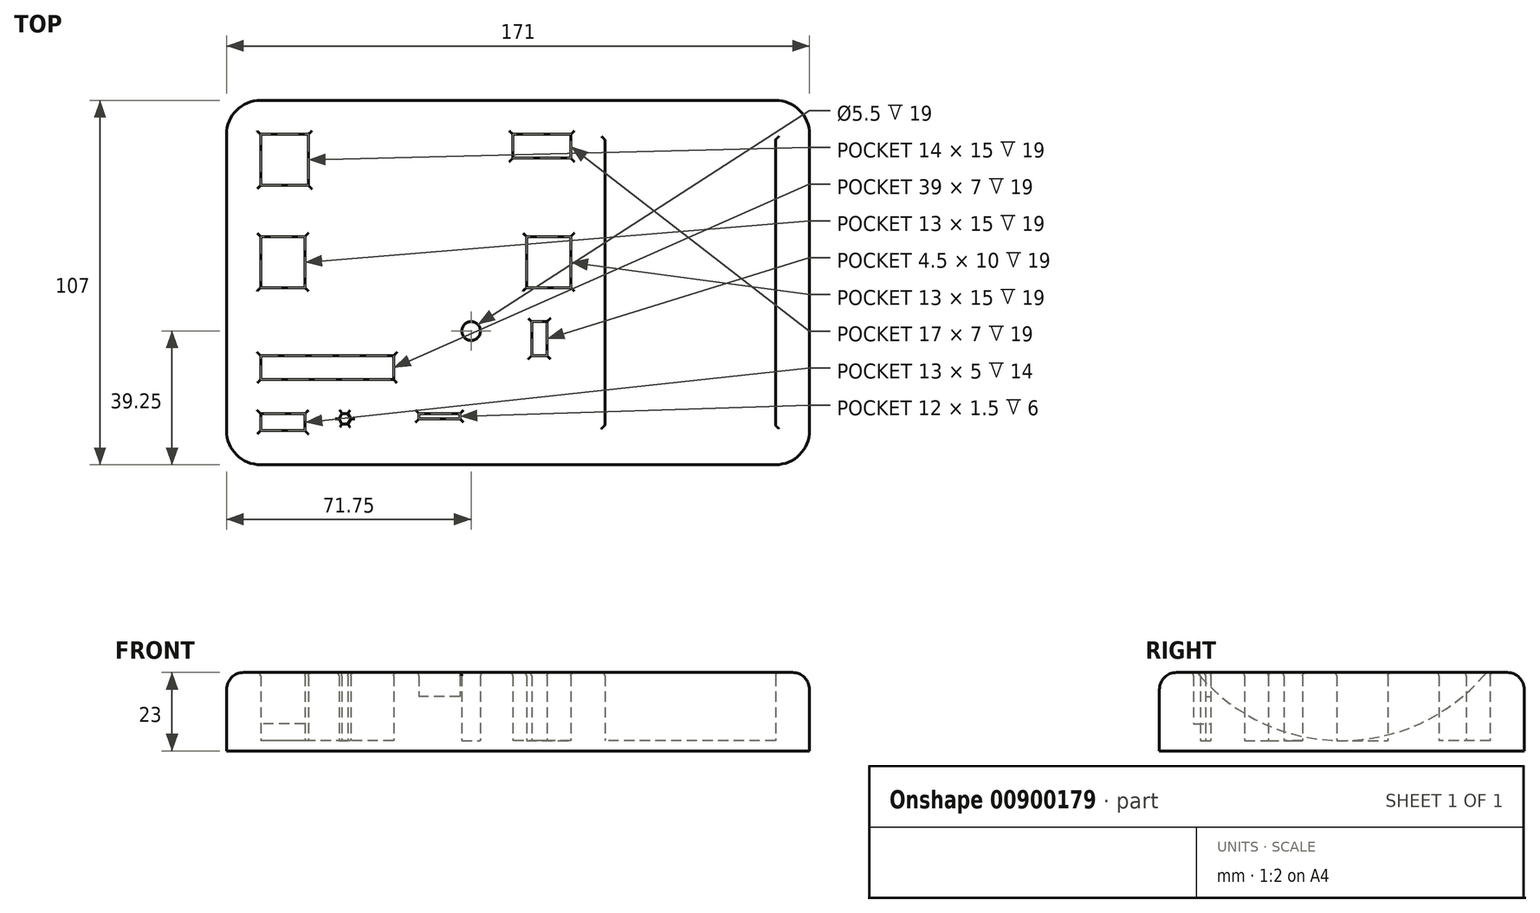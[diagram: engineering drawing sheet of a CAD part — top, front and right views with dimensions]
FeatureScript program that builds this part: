
annotation { "Feature Type Name" : "Feature", "Feature Type Description" : "" }
export const myFeature = defineFeature(function(context is Context, id is Id, definition is map)
    precondition{}
    {
        {
            var Q0;
            Q0=qCreatedBy(makeId("Top.planeOp"),FACE);
            var sketch = newSketch(context, id + "F0", { "sketchPlane" : qUnion([Q0])});
            skLineSegment(sketch, "E0.bottom", {"start": v(0, 0) * mm, "end": v(111, 0) * mm});
            skLineSegment(sketch, "E0.top", {"start": v(0, 107) * mm, "end": v(111, 107) * mm});
            skLineSegment(sketch, "E0.left", {"start": v(0, 0) * mm, "end": v(0, 107) * mm});
            skLineSegment(sketch, "E0.right", {"start": v(111, 0) * mm, "end": v(111, 107) * mm});
            skLineSegment(sketch, "E1.bottom", {"start": v(10, 82) * mm, "end": v(24, 82) * mm});
            skLineSegment(sketch, "E1.top", {"start": v(10, 97) * mm, "end": v(24, 97) * mm});
            skLineSegment(sketch, "E1.left", {"start": v(10, 82) * mm, "end": v(10, 97) * mm});
            skLineSegment(sketch, "E1.right", {"start": v(24, 82) * mm, "end": v(24, 97) * mm});
            skLineSegment(sketch, "E2.bottom", {"start": v(84, 90) * mm, "end": v(101, 90) * mm});
            skLineSegment(sketch, "E2.top", {"start": v(84, 97) * mm, "end": v(101, 97) * mm});
            skLineSegment(sketch, "E2.left", {"start": v(84, 90) * mm, "end": v(84, 97) * mm});
            skLineSegment(sketch, "E2.right", {"start": v(101, 90) * mm, "end": v(101, 97) * mm});
            skLineSegment(sketch, "E3.bottom", {"start": v(10, 32) * mm, "end": v(49, 32) * mm});
            skLineSegment(sketch, "E3.top", {"start": v(10, 25) * mm, "end": v(49, 25) * mm});
            skLineSegment(sketch, "E3.left", {"start": v(10, 32) * mm, "end": v(10, 25) * mm});
            skLineSegment(sketch, "E3.right", {"start": v(49, 32) * mm, "end": v(49, 25) * mm});
            skLineSegment(sketch, "E4.bottom", {"start": v(10, 67) * mm, "end": v(23, 67) * mm});
            skLineSegment(sketch, "E4.top", {"start": v(10, 52) * mm, "end": v(23, 52) * mm});
            skLineSegment(sketch, "E4.left", {"start": v(10, 67) * mm, "end": v(10, 52) * mm});
            skLineSegment(sketch, "E4.right", {"start": v(23, 67) * mm, "end": v(23, 52) * mm});
            skLineSegment(sketch, "E5.bottom", {"start": v(101, 67) * mm, "end": v(88, 67) * mm});
            skLineSegment(sketch, "E5.top", {"start": v(101, 52) * mm, "end": v(88, 52) * mm});
            skLineSegment(sketch, "E5.left", {"start": v(101, 67) * mm, "end": v(101, 52) * mm});
            skLineSegment(sketch, "E5.right", {"start": v(88, 67) * mm, "end": v(88, 52) * mm});
            skCircle(sketch, "E6", {"center": v(71.75, 39.25) * mm, "radius": 2.75 * mm});
            skLineSegment(sketch, "E7.bottom", {"start": v(89.5, 42) * mm, "end": v(94, 42) * mm});
            skLineSegment(sketch, "E7.top", {"start": v(89.5, 32) * mm, "end": v(94, 32) * mm});
            skLineSegment(sketch, "E7.left", {"start": v(89.5, 42) * mm, "end": v(89.5, 32) * mm});
            skLineSegment(sketch, "E7.right", {"start": v(94, 42) * mm, "end": v(94, 32) * mm});
            skLineSegment(sketch, "E8.bottom", {"start": v(10, 15) * mm, "end": v(23, 15) * mm});
            skLineSegment(sketch, "E8.top", {"start": v(10, 10) * mm, "end": v(23, 10) * mm});
            skLineSegment(sketch, "E8.left", {"start": v(10, 15) * mm, "end": v(10, 10) * mm});
            skLineSegment(sketch, "E8.right", {"start": v(23, 15) * mm, "end": v(23, 10) * mm});
            skCircle(sketch, "E9.cCircle", {"center": v(34.73, 13.5) * mm, "radius": 1.5 * mm, "construction": true});
            skLineSegment(sketch, "E9.0", {"start": v(36.46, 13.5) * mm, "end": v(35.6, 12) * mm});
            skLineSegment(sketch, "E9.1", {"start": v(35.6, 12) * mm, "end": v(33.87, 12) * mm});
            skLineSegment(sketch, "E9.2", {"start": v(33.87, 12) * mm, "end": v(33, 13.5) * mm});
            skLineSegment(sketch, "E9.3", {"start": v(33, 13.5) * mm, "end": v(33.87, 15) * mm});
            skLineSegment(sketch, "E9.4", {"start": v(33.87, 15) * mm, "end": v(35.6, 15) * mm});
            skLineSegment(sketch, "E9.5", {"start": v(35.6, 15) * mm, "end": v(36.46, 13.5) * mm});
            skPoint(sketch, "E9.0.midPoint", {"position": v(36.03, 12.75) * mm});
            skLineSegment(sketch, "E10.bottom", {"start": v(56.46, 15) * mm, "end": v(68.46, 15) * mm});
            skLineSegment(sketch, "E10.top", {"start": v(56.46, 13.5) * mm, "end": v(68.46, 13.5) * mm});
            skLineSegment(sketch, "E10.left", {"start": v(56.46, 15) * mm, "end": v(56.46, 13.5) * mm});
            skLineSegment(sketch, "E10.right", {"start": v(68.46, 15) * mm, "end": v(68.46, 13.5) * mm});
            skSolve(sketch);
        }
        {
            var Q0;
            Q0=makeQuery(id+"F0.imprint","IMPRINT",FACE,{"disambiguationData":[TD([[makeQuery(id+"F0.imprint","IMPRINT",EDGE,{"derivedFrom":sQuery(id+"F0.wireOp",EDGE,"E0.bottom")}),1.0]])]});
            extrude(context, id + "F1", {"entities" : qUnion([Q0]), "depth" : 23 * mm, "offsetDistance" : 25 * mm});
        }
        {
            var Q0;
            Q0=makeQuery(id+"F1.opExtrude","CAP_FACE",FACE,{"disambiguationData":[OSD([sQuery(id+"F0.wireOp",EDGE,"E0.bottom"),sQuery(id+"F0.wireOp",EDGE,"E0.top"),sQuery(id+"F0.wireOp",EDGE,"E0.left"),sQuery(id+"F0.wireOp",EDGE,"E0.right"),sQuery(id+"F0.wireOp",EDGE,"E1.bottom"),sQuery(id+"F0.wireOp",EDGE,"E1.top"),sQuery(id+"F0.wireOp",EDGE,"E1.left"),sQuery(id+"F0.wireOp",EDGE,"E1.right"),sQuery(id+"F0.wireOp",EDGE,"E2.bottom"),sQuery(id+"F0.wireOp",EDGE,"E2.top"),sQuery(id+"F0.wireOp",EDGE,"E2.left"),sQuery(id+"F0.wireOp",EDGE,"E2.right"),sQuery(id+"F0.wireOp",EDGE,"E3.bottom"),sQuery(id+"F0.wireOp",EDGE,"E3.top"),sQuery(id+"F0.wireOp",EDGE,"E3.left"),sQuery(id+"F0.wireOp",EDGE,"E3.right"),sQuery(id+"F0.wireOp",EDGE,"E4.bottom"),sQuery(id+"F0.wireOp",EDGE,"E4.top"),sQuery(id+"F0.wireOp",EDGE,"E4.left"),sQuery(id+"F0.wireOp",EDGE,"E4.right"),sQuery(id+"F0.wireOp",EDGE,"E5.bottom"),sQuery(id+"F0.wireOp",EDGE,"E5.top"),sQuery(id+"F0.wireOp",EDGE,"E5.left"),sQuery(id+"F0.wireOp",EDGE,"E5.right"),sQuery(id+"F0.wireOp",EDGE,"E6"),sQuery(id+"F0.wireOp",EDGE,"E7.bottom"),sQuery(id+"F0.wireOp",EDGE,"E7.top"),sQuery(id+"F0.wireOp",EDGE,"E7.left"),sQuery(id+"F0.wireOp",EDGE,"E7.right"),sQuery(id+"F0.wireOp",EDGE,"E8.bottom"),sQuery(id+"F0.wireOp",EDGE,"E8.top"),sQuery(id+"F0.wireOp",EDGE,"E8.left"),sQuery(id+"F0.wireOp",EDGE,"E8.right"),sQuery(id+"F0.wireOp",EDGE,"E9.0"),sQuery(id+"F0.wireOp",EDGE,"E9.1"),sQuery(id+"F0.wireOp",EDGE,"E9.2"),sQuery(id+"F0.wireOp",EDGE,"E9.3"),sQuery(id+"F0.wireOp",EDGE,"E9.4"),sQuery(id+"F0.wireOp",EDGE,"E9.5"),sQuery(id+"F0.wireOp",EDGE,"E10.bottom"),sQuery(id+"F0.wireOp",EDGE,"E10.top"),sQuery(id+"F0.wireOp",EDGE,"E10.left"),sQuery(id+"F0.wireOp",EDGE,"E10.right")])],"isStart":true});
            var sketch = newSketch(context, id + "F2", { "sketchPlane" : qUnion([Q0])});
            skLineSegment(sketch, "E11.0", {"start": v(0, 0) * mm, "end": v(111, 0) * mm});
            skLineSegment(sketch, "E12.0", {"start": v(111, 0) * mm, "end": v(111, -107) * mm});
            skLineSegment(sketch, "E13.0", {"start": v(0, -107) * mm, "end": v(111, -107) * mm});
            skLineSegment(sketch, "E14.0", {"start": v(0, 0) * mm, "end": v(0, -107) * mm});
            skSolve(sketch);
        }
        {
            var Q0;
            Q0 = qSketchRegion(id + "F2", true);
            extrude(context, id + "F3", {"entities" : qUnion([Q0]), "operationType" : NewBodyOperationType.ADD, "oppositeDirection" : true, "depth" : 3 * mm, "offsetDistance" : 25 * mm});
        }
        {
            var Q0;
            Q0=makeQuery(id+"F3.boolean.opBoolean","SPLIT",FACE,{"disambiguationData":[TD([makeQuery(id+"F1.opExtrude","SWEPT_FACE",FACE,{"disambiguationData":[OSD([sQuery(id+"F0.wireOp",EDGE,"E8.bottom")])]})])],"derivedFrom":makeQuery(id+"F3.opExtrude","CAP_FACE",FACE,{"disambiguationData":[OSD([sQuery(id+"F2.wireOp",EDGE,"E11.0"),sQuery(id+"F2.wireOp",EDGE,"E12.0"),sQuery(id+"F2.wireOp",EDGE,"E13.0"),sQuery(id+"F2.wireOp",EDGE,"E14.0")])],"isStart":false})});
            extrude(context, id + "F4", {"entities" : qUnion([Q0]), "operationType" : NewBodyOperationType.ADD, "depth" : 5 * mm, "offsetDistance" : 25 * mm});
        }
        {
            var Q0;
            Q0=makeQuery(id+"F3.boolean.opBoolean","SPLIT",FACE,{"disambiguationData":[TD([makeQuery(id+"F1.opExtrude","SWEPT_FACE",FACE,{"disambiguationData":[OSD([sQuery(id+"F0.wireOp",EDGE,"E10.bottom")])]})])],"derivedFrom":makeQuery(id+"F3.opExtrude","CAP_FACE",FACE,{"disambiguationData":[OSD([sQuery(id+"F2.wireOp",EDGE,"E11.0"),sQuery(id+"F2.wireOp",EDGE,"E12.0"),sQuery(id+"F2.wireOp",EDGE,"E13.0"),sQuery(id+"F2.wireOp",EDGE,"E14.0")])],"isStart":false})});
            extrude(context, id + "F5", {"entities" : qUnion([Q0]), "operationType" : NewBodyOperationType.ADD, "depth" : 13 * mm, "offsetDistance" : 25 * mm});
        }
        {
            var Q0;
            Q0=makeQuery(id+"F1.opExtrude","SWEPT_FACE",FACE,{"disambiguationData":[OSD([sQuery(id+"F0.wireOp",EDGE,"E0.right")])]});
            var sketch = newSketch(context, id + "F6", { "sketchPlane" : qUnion([Q0])});
            skLineSegment(sketch, "E15.bottom", {"start": v(0, 23) * mm, "end": v(11.07, 23) * mm});
            skLineSegment(sketch, "E15.top", {"start": v(0, 0) * mm, "end": v(107, 0) * mm});
            skLineSegment(sketch, "E15.left", {"start": v(0, 23) * mm, "end": v(0, 0) * mm});
            skLineSegment(sketch, "E15.right", {"start": v(107, 23) * mm, "end": v(107, 0) * mm});
            skArc(sketch, "E16", {"start": v(11.07, 23) * mm, "mid": v(53.5, 3) * mm, "end": v(95.93, 23) * mm});
            skPoint(sketch, "E16.centerSnap0", {"position": v(53.5, 23) * mm});
            skLineSegment(sketch, "E17.trimOffspring", {"start": v(95.93, 23) * mm, "end": v(107, 23) * mm});
            skSolve(sketch);
        }
        {
            var Q0;
            Q0=makeQuery(id+"F6.imprint","IMPRINT",FACE,{"disambiguationData":[TD([[makeQuery(id+"F6.imprint","IMPRINT",EDGE,{"derivedFrom":sQuery(id+"F6.wireOp",EDGE,"E15.bottom")}),-1.0]])]});
            extrude(context, id + "F7", {"entities" : qUnion([Q0]), "operationType" : NewBodyOperationType.ADD, "depth" : 50 * mm, "offsetDistance" : 25 * mm});
        }
        {
            var Q0;
            Q0=makeQuery(id+"F7.opExtrude","CAP_FACE",FACE,{"disambiguationData":[OSD([sQuery(id+"F6.wireOp",EDGE,"E15.bottom"),sQuery(id+"F6.wireOp",EDGE,"E15.top"),sQuery(id+"F6.wireOp",EDGE,"E15.left"),sQuery(id+"F6.wireOp",EDGE,"E15.right"),sQuery(id+"F6.wireOp",EDGE,"E16"),sQuery(id+"F6.wireOp",EDGE,"E17.trimOffspring")])],"isStart":false});
            var sketch = newSketch(context, id + "F8", { "sketchPlane" : qUnion([Q0])});
            skPoint(sketch, "E18.0", {"position": v(107, 23) * mm});
            skLineSegment(sketch, "E19.bottom", {"start": v(0, 0) * mm, "end": v(107, 0) * mm});
            skLineSegment(sketch, "E19.top", {"start": v(0, 23) * mm, "end": v(107, 23) * mm});
            skLineSegment(sketch, "E19.left", {"start": v(0, 0) * mm, "end": v(0, 23) * mm});
            skLineSegment(sketch, "E19.right", {"start": v(107, 0) * mm, "end": v(107, 23) * mm});
            skSolve(sketch);
        }
        {
            var Q0;
            Q0=makeQuery(id+"F8.imprint","IMPRINT",FACE,{"disambiguationData":[TD([[makeQuery(id+"F8.imprint","IMPRINT",EDGE,{"derivedFrom":sQuery(id+"F8.wireOp",EDGE,"E19.bottom")}),1.0]])]});
            var Q1;
            {var subQ1=makeQuery(id+"F7.opExtrude","CAP_EDGE",EDGE,{"disambiguationData":[OSD([sQuery(id+"F6.wireOp",EDGE,"E16")])],"isStart":false});Q1=makeQuery(id+"F8.imprint","IMPRINT",FACE,{"disambiguationData":[TD([[makeQuery(id+"F8.imprint","IMPRINT",EDGE,{"derivedFrom":subQ1}),1.0]])]});}
            extrude(context, id + "F9", {"entities" : qUnion([Q0, Q1]), "operationType" : NewBodyOperationType.ADD, "depth" : 10 * mm, "offsetDistance" : 25 * mm});
        }
        {
            var Q0;
            Q0=makeQuery(id+"F9.boolean.opBoolean","MERGE",EDGE,{"derivedFrom":[makeQuery(id+"F7.boolean.opBoolean","MERGE",EDGE,{"derivedFrom":[makeQuery(id+"F1.opExtrude","CAP_EDGE",EDGE,{"disambiguationData":[OSD([sQuery(id+"F0.wireOp",EDGE,"E0.top")])],"isStart":false}),makeQuery(id+"F7.opExtrude","SWEPT_EDGE",EDGE,{"disambiguationData":[OSD([sQuery(id+"F6.wireOp",EDGE,"E15.right"),sQuery(id+"F6.wireOp",EDGE,"E17.trimOffspring")])]})]}),makeQuery(id+"F9.opExtrude","SWEPT_EDGE",EDGE,{"disambiguationData":[OSD([sQuery(id+"F8.wireOp",EDGE,"E19.top"),sQuery(id+"F8.wireOp",EDGE,"E19.right")])]})]});
            var Q1;
            Q1=makeQuery(id+"F9.opExtrude","CAP_EDGE",EDGE,{"disambiguationData":[OSD([sQuery(id+"F8.wireOp",EDGE,"E19.top")])],"isStart":false});
            var Q2;
            Q2=makeQuery(id+"F9.boolean.opBoolean","MERGE",EDGE,{"derivedFrom":[makeQuery(id+"F7.boolean.opBoolean","MERGE",EDGE,{"derivedFrom":[makeQuery(id+"F1.opExtrude","CAP_EDGE",EDGE,{"disambiguationData":[OSD([sQuery(id+"F0.wireOp",EDGE,"E0.bottom")])],"isStart":false}),makeQuery(id+"F7.opExtrude","SWEPT_EDGE",EDGE,{"disambiguationData":[OSD([sQuery(id+"F6.wireOp",EDGE,"E15.bottom"),sQuery(id+"F6.wireOp",EDGE,"E15.left")])]})]}),makeQuery(id+"F9.opExtrude","SWEPT_EDGE",EDGE,{"disambiguationData":[OSD([sQuery(id+"F8.wireOp",EDGE,"E19.top"),sQuery(id+"F8.wireOp",EDGE,"E19.left")])]})]});
            var Q3;
            Q3=makeQuery(id+"F1.opExtrude","CAP_EDGE",EDGE,{"disambiguationData":[OSD([sQuery(id+"F0.wireOp",EDGE,"E0.left")])],"isStart":false});
            fillet(context, id + "F10", {"entities" : qUnion([Q0, Q1, Q2, Q3]), "radius" : 5 * mm, "tangentPropagation" : true, "allowEdgeOverflow" : false});
        }
        {
            var Q0;
            Q0=makeQuery(id+"F9.opExtrude","CAP_EDGE",EDGE,{"disambiguationData":[OSD([sQuery(id+"F8.wireOp",EDGE,"E19.right")])],"isStart":false});
            var Q1;
            Q1=makeQuery(id+"F9.opExtrude","CAP_EDGE",EDGE,{"disambiguationData":[OSD([sQuery(id+"F8.wireOp",EDGE,"E19.left")])],"isStart":false});
            var Q2;
            Q2=makeQuery(id+"F1.opExtrude","SWEPT_EDGE",EDGE,{"disambiguationData":[OSD([sQuery(id+"F0.wireOp",EDGE,"E0.bottom"),sQuery(id+"F0.wireOp",EDGE,"E0.left")])]});
            var Q3;
            Q3=makeQuery(id+"F1.opExtrude","SWEPT_EDGE",EDGE,{"disambiguationData":[OSD([sQuery(id+"F0.wireOp",EDGE,"E0.top"),sQuery(id+"F0.wireOp",EDGE,"E0.left")])]});
            fillet(context, id + "F11", {"entities" : qUnion([Q0, Q1, Q2, Q3]), "radius" : 10 * mm, "tangentPropagation" : true, "allowEdgeOverflow" : false});
        }
        {
            var Q0;
            Q0=makeQuery(id+"F9.boolean.opBoolean","MERGE",FACE,{"derivedFrom":[makeQuery(id+"F7.boolean.opBoolean","MERGE",FACE,{"derivedFrom":[makeQuery(id+"F1.opExtrude","CAP_FACE",FACE,{"disambiguationData":[OSD([sQuery(id+"F0.wireOp",EDGE,"E0.bottom"),sQuery(id+"F0.wireOp",EDGE,"E0.top"),sQuery(id+"F0.wireOp",EDGE,"E0.left"),sQuery(id+"F0.wireOp",EDGE,"E0.right"),sQuery(id+"F0.wireOp",EDGE,"E1.bottom"),sQuery(id+"F0.wireOp",EDGE,"E1.top"),sQuery(id+"F0.wireOp",EDGE,"E1.left"),sQuery(id+"F0.wireOp",EDGE,"E1.right"),sQuery(id+"F0.wireOp",EDGE,"E2.bottom"),sQuery(id+"F0.wireOp",EDGE,"E2.top"),sQuery(id+"F0.wireOp",EDGE,"E2.left"),sQuery(id+"F0.wireOp",EDGE,"E2.right"),sQuery(id+"F0.wireOp",EDGE,"E3.bottom"),sQuery(id+"F0.wireOp",EDGE,"E3.top"),sQuery(id+"F0.wireOp",EDGE,"E3.left"),sQuery(id+"F0.wireOp",EDGE,"E3.right"),sQuery(id+"F0.wireOp",EDGE,"E4.bottom"),sQuery(id+"F0.wireOp",EDGE,"E4.top"),sQuery(id+"F0.wireOp",EDGE,"E4.left"),sQuery(id+"F0.wireOp",EDGE,"E4.right"),sQuery(id+"F0.wireOp",EDGE,"E5.bottom"),sQuery(id+"F0.wireOp",EDGE,"E5.top"),sQuery(id+"F0.wireOp",EDGE,"E5.left"),sQuery(id+"F0.wireOp",EDGE,"E5.right"),sQuery(id+"F0.wireOp",EDGE,"E6"),sQuery(id+"F0.wireOp",EDGE,"E7.bottom"),sQuery(id+"F0.wireOp",EDGE,"E7.top"),sQuery(id+"F0.wireOp",EDGE,"E7.left"),sQuery(id+"F0.wireOp",EDGE,"E7.right"),sQuery(id+"F0.wireOp",EDGE,"E8.bottom"),sQuery(id+"F0.wireOp",EDGE,"E8.top"),sQuery(id+"F0.wireOp",EDGE,"E8.left"),sQuery(id+"F0.wireOp",EDGE,"E8.right"),sQuery(id+"F0.wireOp",EDGE,"E9.0"),sQuery(id+"F0.wireOp",EDGE,"E9.1"),sQuery(id+"F0.wireOp",EDGE,"E9.2"),sQuery(id+"F0.wireOp",EDGE,"E9.3"),sQuery(id+"F0.wireOp",EDGE,"E9.4"),sQuery(id+"F0.wireOp",EDGE,"E9.5"),sQuery(id+"F0.wireOp",EDGE,"E10.bottom"),sQuery(id+"F0.wireOp",EDGE,"E10.top"),sQuery(id+"F0.wireOp",EDGE,"E10.left"),sQuery(id+"F0.wireOp",EDGE,"E10.right")])],"isStart":false}),makeQuery(id+"F7.opExtrude","SWEPT_FACE",FACE,{"disambiguationData":[OSD([sQuery(id+"F6.wireOp",EDGE,"E15.bottom")])]}),makeQuery(id+"F7.opExtrude","SWEPT_FACE",FACE,{"disambiguationData":[OSD([sQuery(id+"F6.wireOp",EDGE,"E17.trimOffspring")])]})]}),makeQuery(id+"F9.opExtrude","SWEPT_FACE",FACE,{"disambiguationData":[OSD([sQuery(id+"F8.wireOp",EDGE,"E19.top")])]})]});
            fillet(context, id + "F12", {"entities" : qUnion([Q0]), "radius" : 1 * mm, "tangentPropagation" : true, "allowEdgeOverflow" : false});
        }
    });
